# Revit family: Tub_Filler-DXV-Belshire-D35170980_Series
name_source: partatom
category: Plumbing Fixtures
units: mm (PartAtom-declared; Revit-internal decimal feet)

## family parameters
Cut with Voids When Loaded = No
Host = Face
OmniClass Number = 23.45.05.14.17
OmniClass Title = Showers
Part Type = Normal
Room Calculation Point = No
Round Connector Dimension = Use Diameter
Shared = Yes

## types (4) — shared parameters
ADA Compliant = Yes
ASME A112.18.1/CSA B125.1 = Yes
Assembly Code = D2010900
CEC Compliant = Yes
CW Connection = Yes
CWFU = 1.5
Cold Water Connection Diameter = 3/4"
Cold Water Connection Radius = 3/8"
Default Elevation = 0"
Description = BELSHIRE WALL-MOUNT TUB FILLER WITH LEVER HANDLES
Diverter Outlet Connection = 3/4"
Flow Rate = Hand Shower-1.8 gpm (6.8 L/min) , Tub Filler-4.1 gpm (15.5 L/min)
HW Connection = Yes
HWFU = 1.5
Height = 9 1/2"
Hot Water Connection Diameter = 3/4"
Hot Water Connection Radius = 3/8"
Installation Type = Wallmount
Length = 15 3/4"
Manufacturer = DXV
Mixer Connection = 3/4"
Price = Prices may vary. Please consult Manufacturer Representative for most up-to-date price list.
Product Documentation Link = https://dxv01.blob.core.windows.net
Product Page URL = https://www.dxv.com
Tempered Water Connection = Yes
Tempered Water Connection Diameter = 1/2"
Tempered Water Connection Radius = 1/4"
URL = https://www.dxv.com
Vent Connection = No
WFU = 2
Waste Connection = No
Width = 3 3/4"

## per-type parameters (varying)
| type | Finish | Material |
| D35170980.100 | Cast Brass-DXV-100-Polished Chrome | Cast Brass-DXV-100-Polished Chrome |
| D35170980.150 | Cast Brass-DXV-150-Platinum Nickel | Cast Brass-DXV-150-Platinum Nickel |
| D35170980.144 | Cast Brass-DXV-144-Brushed Nickel | Cast Brass-DXV-144-Brushed Nickel |
| D35170980.427 | Cast Brass-DXV-427-Satin Brass | Cast Brass-DXV-427-Satin Brass |

note: column(s) folded — value = type name in every type: Model

## geometry (parser evidence)
native form markers: Sweep x2
no freeform markers — native parametric forms only
